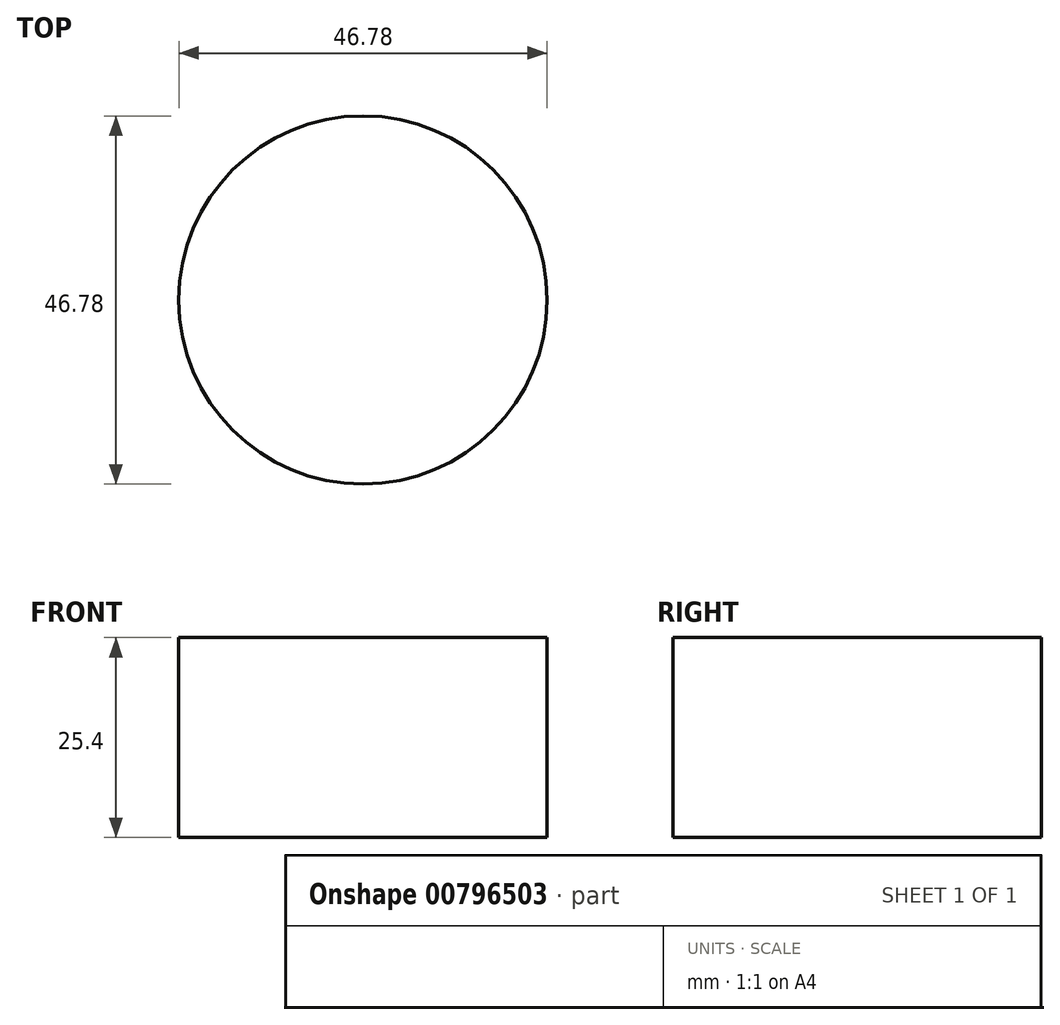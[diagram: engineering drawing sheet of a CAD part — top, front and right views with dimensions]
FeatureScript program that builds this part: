
annotation { "Feature Type Name" : "Feature", "Feature Type Description" : "" }
export const myFeature = defineFeature(function(context is Context, id is Id, definition is map)
    precondition{}
    {
        {
            var Q0;
            Q0=qCreatedBy(makeId("Top.planeOp"),FACE);
            var sketch = newSketch(context, id + "F0", { "sketchPlane" : qUnion([Q0])});
            skCircle(sketch, "E0", {"center": v(0, 0) * mm, "radius": 23.4 * mm});
            skSolve(sketch);
        }
        {
            var Q0;
            Q0=makeQuery(id+"F0.imprint","IMPRINT",FACE,{"disambiguationData":[TD([[makeQuery(id+"F0.imprint","IMPRINT",EDGE,{"derivedFrom":sQuery(id+"F0.wireOp",EDGE,"E0")}),1.0]])]});
            extrude(context, id + "F1", {"entities" : qUnion([Q0]), "depth" : 25.4 * mm, "offsetDistance" : 25.4 * mm});
        }
    });
